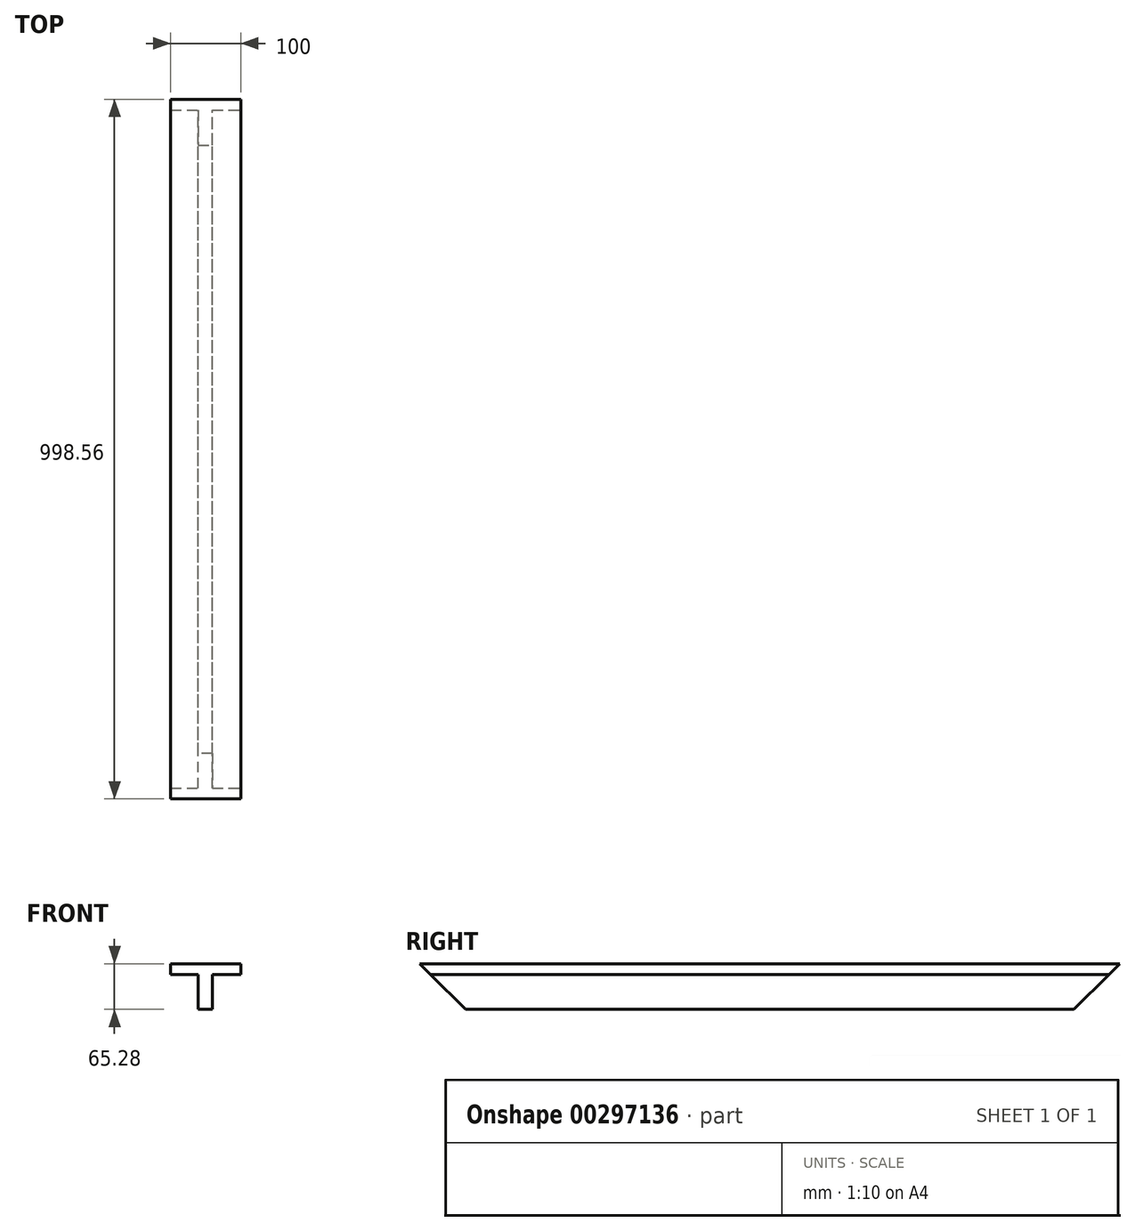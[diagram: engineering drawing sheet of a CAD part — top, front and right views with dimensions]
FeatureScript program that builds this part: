
annotation { "Feature Type Name" : "Feature", "Feature Type Description" : "" }
export const myFeature = defineFeature(function(context is Context, id is Id, definition is map)
    precondition{}
    {
        {
            var Q0;
            Q0=qCreatedBy(makeId("Front.planeOp"),FACE);
            var sketch = newSketch(context, id + "F0", { "sketchPlane" : qUnion([Q0])});
            skLineSegment(sketch, "E0.bottom", {"start": v(50, 7.64) * mm, "end": v(-50, 7.64) * mm});
            skLineSegment(sketch, "E0.top", {"start": v(50, -7.64) * mm, "end": v(-50, -7.64) * mm});
            skLineSegment(sketch, "E0.left", {"start": v(50, 7.64) * mm, "end": v(50, -7.64) * mm});
            skLineSegment(sketch, "E0.right", {"start": v(-50, 7.64) * mm, "end": v(-50, -7.64) * mm});
            skPoint(sketch, "E0.middle", {"position": v(0, 0) * mm});
            skLineSegment(sketch, "E1.bottom", {"start": v(0, -7.64) * mm, "end": v(9.43, -7.64) * mm});
            skLineSegment(sketch, "E2.MirrorCS", {"start": v(-1.13, -7.64) * mm, "end": v(-10.57, -7.64) * mm});
            skLineSegment(sketch, "E3.bottom", {"start": v(9.43, -7.64) * mm, "end": v(-10.57, -7.64) * mm});
            skLineSegment(sketch, "E3.top", {"start": v(9.43, -57.64) * mm, "end": v(-10.57, -57.64) * mm});
            skLineSegment(sketch, "E3.left", {"start": v(9.43, -7.64) * mm, "end": v(9.43, -57.64) * mm});
            skLineSegment(sketch, "E3.right", {"start": v(-10.57, -7.64) * mm, "end": v(-10.57, -57.64) * mm});
            skSolve(sketch);
        }
        {
            var Q0;
            Q0 = qSketchRegion(id + "F0", true);
            extrude(context, id + "F1", {"entities" : qUnion([Q0]), "endBound" : BoundingType.SYMMETRIC, "depth" : 1000 * mm});
        }
        {
            var Q0;
            Q0=makeQuery(id+"F1.opExtrude","CAP_EDGE",EDGE,{"disambiguationData":[OSD([sQuery(id+"F0.wireOp",EDGE,"E3.top")])],"isStart":true});
            chamfer(context, id + "F2", {"entities" : qUnion([Q0]), "width" : 66 * mm, "tangentPropagation" : true});
        }
        {
            var Q0;
            Q0=makeQuery(id+"F1.opExtrude","CAP_EDGE",EDGE,{"disambiguationData":[OSD([sQuery(id+"F0.wireOp",EDGE,"E3.top")])],"isStart":false});
            chamfer(context, id + "F3", {"entities" : qUnion([Q0]), "width" : 66 * mm, "tangentPropagation" : true});
        }
    });
